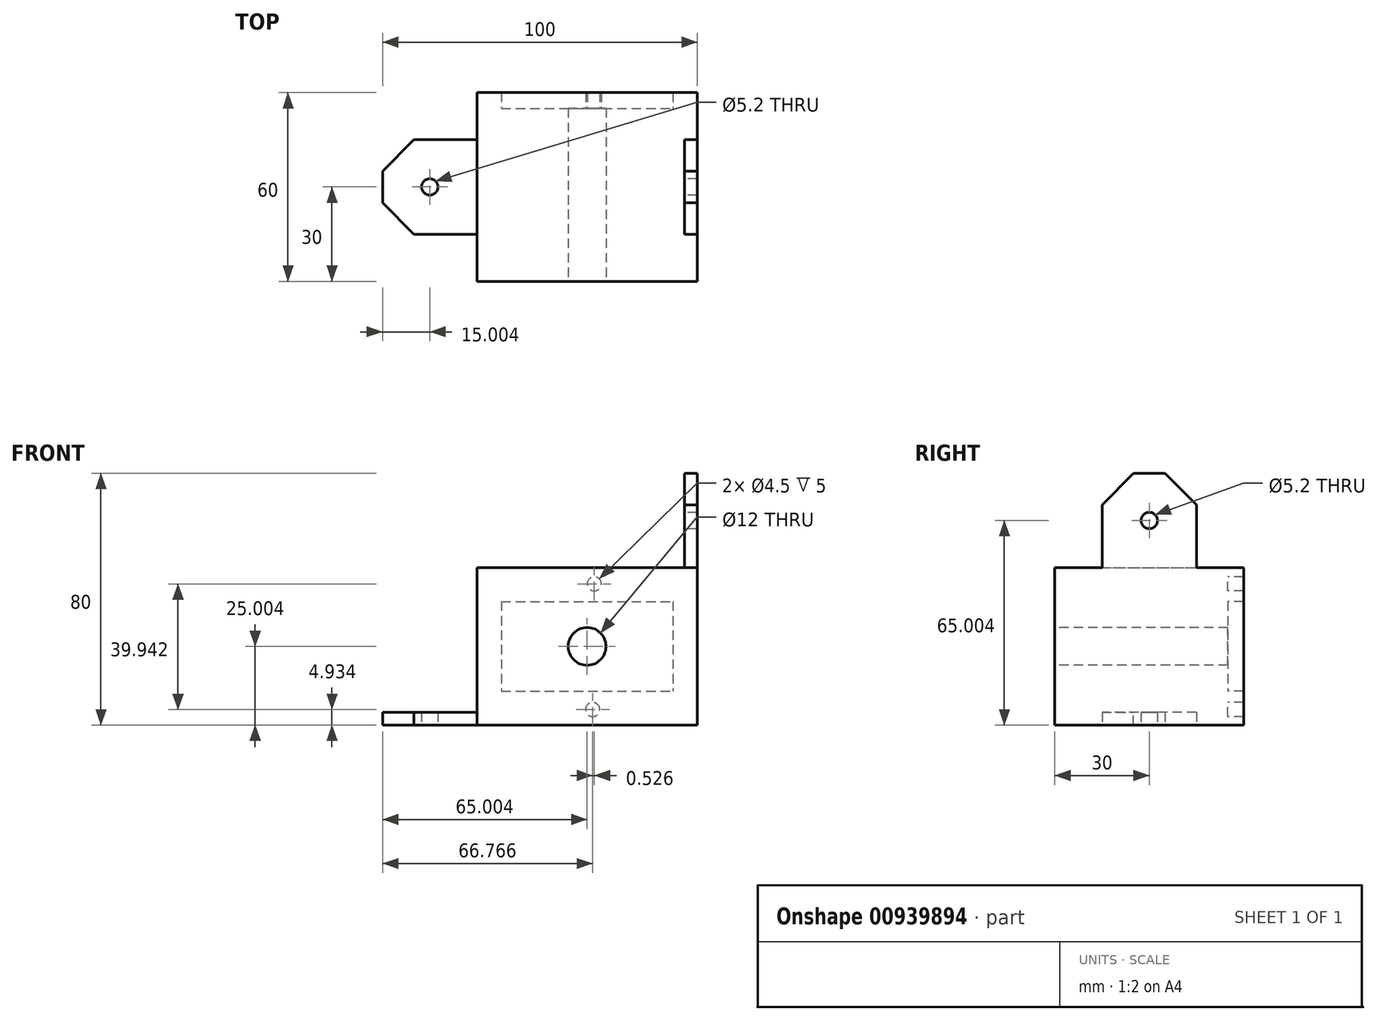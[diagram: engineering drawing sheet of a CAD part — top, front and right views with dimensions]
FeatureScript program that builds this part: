
annotation { "Feature Type Name" : "Feature", "Feature Type Description" : "" }
export const myFeature = defineFeature(function(context is Context, id is Id, definition is map)
    precondition{}
    {
        {
            var Q0;
            Q0=qCreatedBy(makeId("Front.planeOp"),FACE);
            var sketch = newSketch(context, id + "F0", { "sketchPlane" : qUnion([Q0])});
            skLineSegment(sketch, "E0.bottom", {"start": v(-42.53, 32.88) * mm, "end": v(27.47, 32.88) * mm});
            skLineSegment(sketch, "E0.top", {"start": v(-42.53, -17.12) * mm, "end": v(27.47, -17.12) * mm});
            skLineSegment(sketch, "E0.left", {"start": v(-42.53, 32.88) * mm, "end": v(-42.53, -17.12) * mm});
            skLineSegment(sketch, "E0.right", {"start": v(27.47, 32.88) * mm, "end": v(27.47, -17.12) * mm});
            skSolve(sketch);
        }
        {
            var Q0;
            Q0=qCreatedBy(makeId("Front.planeOp"),FACE);
            var sketch = newSketch(context, id + "F1", { "sketchPlane" : qUnion([Q0])});
            skLineSegment(sketch, "E1.bottom", {"start": v(-34.78, 22.13) * mm, "end": v(19.72, 22.13) * mm});
            skLineSegment(sketch, "E1.top", {"start": v(-34.78, -6.37) * mm, "end": v(19.72, -6.37) * mm});
            skLineSegment(sketch, "E1.left", {"start": v(-34.78, 22.13) * mm, "end": v(-34.78, -6.37) * mm});
            skLineSegment(sketch, "E1.right", {"start": v(19.72, 22.13) * mm, "end": v(19.72, -6.37) * mm});
            skCircle(sketch, "E2", {"center": v(-5.24, 27.76) * mm, "radius": 2.25 * mm});
            skCircle(sketch, "E3", {"center": v(-5.76, -12.19) * mm, "radius": 2.25 * mm});
            skSolve(sketch);
        }
        {
            var Q0;
            Q0 = qSketchRegion(id + "F0", true);
            extrude(context, id + "F2", {"entities" : qUnion([Q0]), "depth" : 60 * mm, "offsetDistance" : 25 * mm});
        }
        {
            var Q0;
            Q0 = qSketchRegion(id + "F1", true);
            extrude(context, id + "F3", {"entities" : qUnion([Q0]), "operationType" : NewBodyOperationType.REMOVE, "endBound" : BoundingType.SYMMETRIC, "oppositeDirection" : true, "depth" : 10 * mm, "offsetDistance" : 25 * mm});
        }
        {
            var Q0;
            Q0=makeQuery(id+"F2.opExtrude","CAP_FACE",FACE,{"disambiguationData":[OSD([sQuery(id+"F0.wireOp",EDGE,"E0.bottom"),sQuery(id+"F0.wireOp",EDGE,"E0.top"),sQuery(id+"F0.wireOp",EDGE,"E0.left"),sQuery(id+"F0.wireOp",EDGE,"E0.right")])],"isStart":false});
            var sketch = newSketch(context, id + "F4", { "sketchPlane" : qUnion([Q0])});
            skCircle(sketch, "E4", {"center": v(-7.53, 7.88) * mm, "radius": 6 * mm});
            skSolve(sketch);
        }
        {
            var Q0;
            Q0=makeQuery(id+"F4.imprint","IMPRINT",FACE,{"disambiguationData":[TD([[makeQuery(id+"F4.imprint","IMPRINT",EDGE,{"derivedFrom":sQuery(id+"F4.wireOp",EDGE,"E4")}),1.0]])]});
            var Q1;
            Q1=makeQuery(id+"F2.opExtrude","CAP_FACE",FACE,{"disambiguationData":[OSD([sQuery(id+"F0.wireOp",EDGE,"E0.bottom"),sQuery(id+"F0.wireOp",EDGE,"E0.top"),sQuery(id+"F0.wireOp",EDGE,"E0.left"),sQuery(id+"F0.wireOp",EDGE,"E0.right")])],"isStart":true});
            extrude(context, id + "F5", {"entities" : qUnion([Q0]), "operationType" : NewBodyOperationType.REMOVE, "endBound" : BoundingType.UP_TO_SURFACE, "oppositeDirection" : true, "depth" : 25 * mm, "endBoundEntityFace" : qUnion([Q1]), "offsetDistance" : 25 * mm});
        }
        {
            var Q0;
            Q0=makeQuery(id+"F2.opExtrude","SWEPT_FACE",FACE,{"disambiguationData":[OSD([sQuery(id+"F0.wireOp",EDGE,"E0.bottom")])]});
            var sketch = newSketch(context, id + "F6", { "sketchPlane" : qUnion([Q0])});
            skLineSegment(sketch, "E5.bottom", {"start": v(23.47, -45) * mm, "end": v(27.47, -45) * mm});
            skLineSegment(sketch, "E5.top", {"start": v(23.47, -15) * mm, "end": v(27.47, -15) * mm});
            skLineSegment(sketch, "E5.left", {"start": v(23.47, -45) * mm, "end": v(23.47, -15) * mm});
            skLineSegment(sketch, "E5.right", {"start": v(27.47, -45) * mm, "end": v(27.47, -15) * mm});
            skSolve(sketch);
        }
        {
            var Q0;
            Q0=makeQuery(id+"F6.imprint","IMPRINT",FACE,{"disambiguationData":[TD([[makeQuery(id+"F6.imprint","IMPRINT",EDGE,{"derivedFrom":sQuery(id+"F6.wireOp",EDGE,"E5.bottom")}),1.0]])]});
            extrude(context, id + "F7", {"entities" : qUnion([Q0]), "operationType" : NewBodyOperationType.ADD, "depth" : 30 * mm, "offsetDistance" : 25 * mm});
        }
        {
            var Q0;
            Q0=makeQuery(id+"F2.opExtrude","SWEPT_FACE",FACE,{"disambiguationData":[OSD([sQuery(id+"F0.wireOp",EDGE,"E0.left")])]});
            var sketch = newSketch(context, id + "F8", { "sketchPlane" : qUnion([Q0])});
            skLineSegment(sketch, "E6.bottom", {"start": v(15, -13.12) * mm, "end": v(45, -13.12) * mm});
            skLineSegment(sketch, "E6.top", {"start": v(15, -17.12) * mm, "end": v(45, -17.12) * mm});
            skLineSegment(sketch, "E6.left", {"start": v(15, -13.12) * mm, "end": v(15, -17.12) * mm});
            skLineSegment(sketch, "E6.right", {"start": v(45, -13.12) * mm, "end": v(45, -17.12) * mm});
            skSolve(sketch);
        }
        {
            var Q0;
            Q0=makeQuery(id+"F8.imprint","IMPRINT",FACE,{"disambiguationData":[TD([[makeQuery(id+"F8.imprint","IMPRINT",EDGE,{"derivedFrom":sQuery(id+"F8.wireOp",EDGE,"E6.bottom")}),-1.0]])]});
            extrude(context, id + "F9", {"entities" : qUnion([Q0]), "operationType" : NewBodyOperationType.ADD, "depth" : 30 * mm, "offsetDistance" : 25 * mm});
        }
        {
            var Q0;
            Q0=makeQuery(id+"F7.opExtrude","SWEPT_FACE",FACE,{"disambiguationData":[OSD([sQuery(id+"F6.wireOp",EDGE,"E5.left")])]});
            var sketch = newSketch(context, id + "F10", { "sketchPlane" : qUnion([Q0])});
            skPoint(sketch, "E7", {"position": v(30, 47.88) * mm});
            skCircle(sketch, "E8", {"center": v(30, 47.88) * mm, "radius": 2.6 * mm});
            skSolve(sketch);
        }
        {
            var Q0;
            Q0=makeQuery(id+"F10.imprint","IMPRINT",FACE,{"disambiguationData":[TD([[makeQuery(id+"F10.imprint","IMPRINT",EDGE,{"derivedFrom":sQuery(id+"F10.wireOp",EDGE,"E8")}),1.0]])]});
            extrude(context, id + "F11", {"entities" : qUnion([Q0]), "operationType" : NewBodyOperationType.REMOVE, "endBound" : BoundingType.SYMMETRIC, "oppositeDirection" : true, "depth" : 25 * mm, "offsetDistance" : 25 * mm});
        }
        {
            var Q0;
            Q0=makeQuery(id+"F9.opExtrude","SWEPT_FACE",FACE,{"disambiguationData":[OSD([sQuery(id+"F8.wireOp",EDGE,"E6.bottom")])]});
            var sketch = newSketch(context, id + "F12", { "sketchPlane" : qUnion([Q0])});
            skPoint(sketch, "E9", {"position": v(-57.53, -30) * mm});
            skCircle(sketch, "E10", {"center": v(-57.53, -30) * mm, "radius": 2.6 * mm});
            skSolve(sketch);
        }
        {
            var Q0;
            Q0=makeQuery(id+"F12.imprint","IMPRINT",FACE,{"disambiguationData":[TD([[makeQuery(id+"F12.imprint","IMPRINT",EDGE,{"derivedFrom":sQuery(id+"F12.wireOp",EDGE,"E10")}),1.0]])]});
            var Q1;
            Q1=sQuery(id+"F12.wireOp",EDGE,"E10");
            extrude(context, id + "F13", {"entities" : qUnion([Q0]), "operationType" : NewBodyOperationType.REMOVE, "surfaceEntities" : qUnion([Q1]), "endBound" : BoundingType.SYMMETRIC, "depth" : 25 * mm, "offsetDistance" : 25 * mm});
        }
        {
            var Q0;
            Q0=makeQuery(id+"F7.opExtrude","CAP_EDGE",EDGE,{"disambiguationData":[OSD([sQuery(id+"F6.wireOp",EDGE,"E5.top")])],"isStart":false});
            var Q1;
            Q1=makeQuery(id+"F7.opExtrude","CAP_EDGE",EDGE,{"disambiguationData":[OSD([sQuery(id+"F6.wireOp",EDGE,"E5.bottom")])],"isStart":false});
            var Q2;
            Q2=makeQuery(id+"F9.opExtrude","CAP_EDGE",EDGE,{"disambiguationData":[OSD([sQuery(id+"F8.wireOp",EDGE,"E6.left")])],"isStart":false});
            var Q3;
            Q3=makeQuery(id+"F9.opExtrude","CAP_EDGE",EDGE,{"disambiguationData":[OSD([sQuery(id+"F8.wireOp",EDGE,"E6.right")])],"isStart":false});
            chamfer(context, id + "F14", {"entities" : qUnion([Q0, Q1, Q2, Q3]), "width" : 10 * mm, "tangentPropagation" : true});
        }
    });
